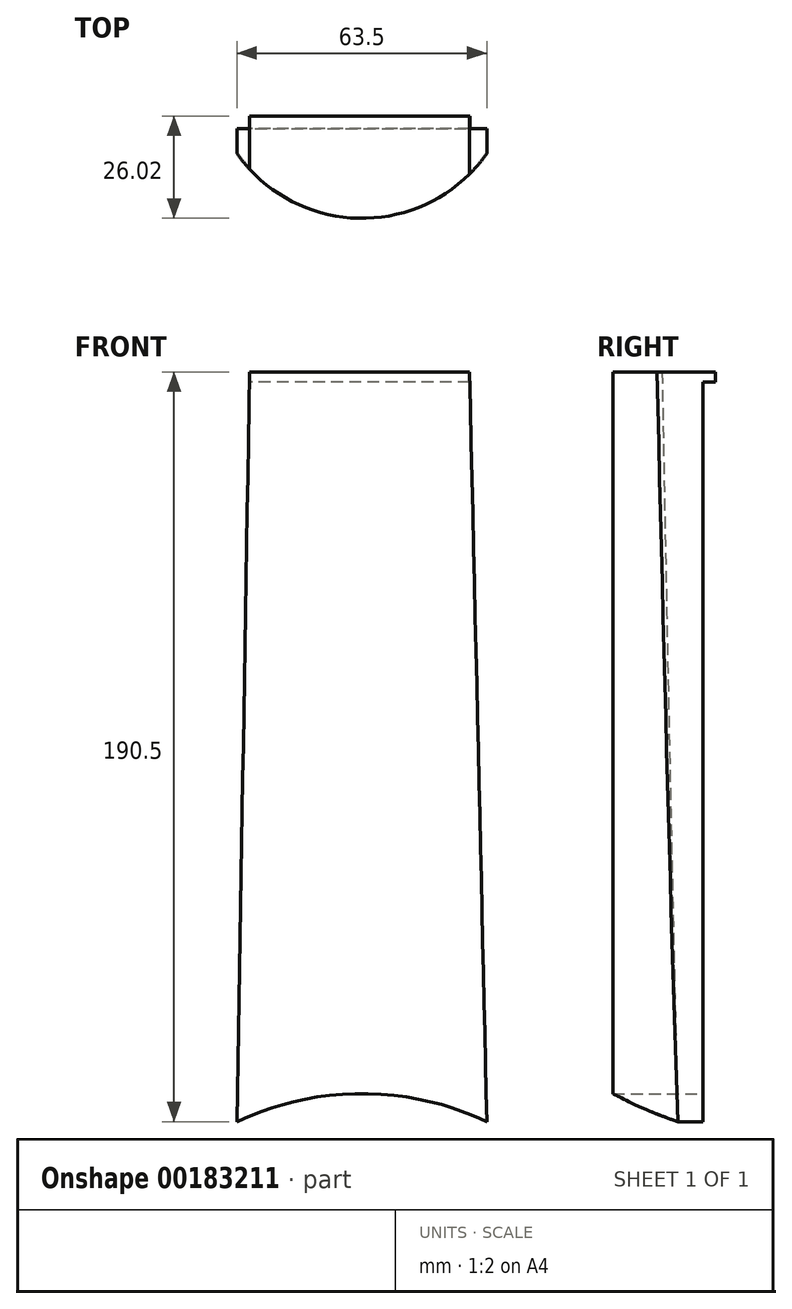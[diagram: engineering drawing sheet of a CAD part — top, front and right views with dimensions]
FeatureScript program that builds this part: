
annotation { "Feature Type Name" : "Feature", "Feature Type Description" : "" }
export const myFeature = defineFeature(function(context is Context, id is Id, definition is map)
    precondition{}
    {
        {
            var Q0;
            Q0=qCreatedBy(makeId("Top.planeOp"),FACE);
            var sketch = newSketch(context, id + "F0", { "sketchPlane" : qUnion([Q0])});
            skLineSegment(sketch, "E0.bottom", {"start": v(-12.13, 0) * mm, "end": v(51.37, 0) * mm});
            skLineSegment(sketch, "E0.top", {"start": v(-12.13, 6.35) * mm, "end": v(51.37, 6.35) * mm});
            skLineSegment(sketch, "E0.left", {"start": v(-12.13, 0) * mm, "end": v(-12.13, 6.35) * mm});
            skLineSegment(sketch, "E0.right", {"start": v(51.37, 0) * mm, "end": v(51.37, 6.35) * mm});
            skArc(sketch, "E1", {"start": v(-12.13, 0) * mm, "mid": v(19.62, -16.5) * mm, "end": v(51.37, 0) * mm});
            skSolve(sketch);
        }
        {
            var Q0;
            Q0=makeQuery(id+"F0.imprint","IMPRINT",FACE,{"disambiguationData":[TD([[makeQuery(id+"F0.imprint","IMPRINT",EDGE,{"derivedFrom":sQuery(id+"F0.wireOp",EDGE,"E0.bottom")}),-1.0]])]});
            var Q1;
            Q1=makeQuery(id+"F0.imprint","IMPRINT",FACE,{"disambiguationData":[TD([[makeQuery(id+"F0.imprint","IMPRINT",EDGE,{"derivedFrom":sQuery(id+"F0.wireOp",EDGE,"E0.bottom")}),1.0]])]});
            extrude(context, id + "F1", {"entities" : qUnion([Q0, Q1]), "depth" : 190.5 * mm});
        }
        {
            var Q0;
            Q0=makeQuery(id+"F1.opExtrude","SWEPT_FACE",FACE,{"disambiguationData":[OSD([sQuery(id+"F0.wireOp",EDGE,"E0.top")])]});
            var sketch = newSketch(context, id + "F2", { "sketchPlane" : qUnion([Q0])});
            skLineSegment(sketch, "E2", {"start": v(-51.37, 0) * mm, "end": v(-46.95, 190.5) * mm});
            skLineSegment(sketch, "E3", {"start": v(-46.95, 190.5) * mm, "end": v(8.92, 190.5) * mm});
            skLineSegment(sketch, "E4", {"start": v(8.92, 190.5) * mm, "end": v(12.13, 0) * mm});
            skSolve(sketch);
        }
        {
            var Q0;
            Q0 = qSketchRegion(id + "F2", true);
            var Q1;
            {var subQ0=sQuery(id+"F2.wireOp",EDGE,"E2");Q1=makeQuery(id+"F2.imprint","IMPRINT",FACE,{"disambiguationData":[TD([[makeQuery(id+"F2.imprint","IMPRINT",EDGE,{"derivedFrom":subQ0}),1.0]])]});}
            var Q2;
            {var subQ0=sQuery(id+"F2.wireOp",EDGE,"E4");Q2=makeQuery(id+"F2.imprint","IMPRINT",FACE,{"disambiguationData":[TD([[makeQuery(id+"F2.imprint","IMPRINT",EDGE,{"derivedFrom":subQ0}),1.0]])]});}
            extrude(context, id + "F3", {"entities" : qUnion([Q0, Q1, Q2]), "operationType" : NewBodyOperationType.REMOVE, "oppositeDirection" : true, "depth" : 25.4 * mm});
        }
        {
            var Q0;
            Q0=makeQuery(id+"F1.opExtrude","SWEPT_FACE",FACE,{"disambiguationData":[OSD([sQuery(id+"F0.wireOp",EDGE,"E0.top")])]});
            var sketch = newSketch(context, id + "F4", { "sketchPlane" : qUnion([Q0])});
            skArc(sketch, "E5", {"start": v(12.13, 0) * mm, "mid": v(-19.62, 7.1) * mm, "end": v(-51.37, 0) * mm});
            skLineSegment(sketch, "E6", {"start": v(12.13, 0) * mm, "end": v(-51.37, 0) * mm});
            skSolve(sketch);
        }
        {
            var Q0;
            Q0=makeQuery(id+"F4.imprint","IMPRINT",FACE,{"disambiguationData":[TD([[makeQuery(id+"F4.imprint","IMPRINT",EDGE,{"derivedFrom":sQuery(id+"F4.wireOp",EDGE,"E5")}),1.0]])]});
            extrude(context, id + "F5", {"entities" : qUnion([Q0]), "operationType" : NewBodyOperationType.REMOVE, "oppositeDirection" : true, "depth" : 25.4 * mm});
        }
        {
            var Q0;
            Q0=makeQuery(id+"F1.opExtrude","SWEPT_FACE",FACE,{"disambiguationData":[OSD([sQuery(id+"F0.wireOp",EDGE,"E0.top")])]});
            var sketch = newSketch(context, id + "F6", { "sketchPlane" : qUnion([Q0])});
            skLineSegment(sketch, "E7", {"start": v(-46.95, 190.5) * mm, "end": v(-47.01, 187.96) * mm});
            skLineSegment(sketch, "E8", {"start": v(-47.01, 187.96) * mm, "end": v(8.96, 187.96) * mm});
            skLineSegment(sketch, "E9", {"start": v(8.96, 187.96) * mm, "end": v(8.92, 190.5) * mm});
            skLineSegment(sketch, "E10", {"start": v(8.92, 190.5) * mm, "end": v(-46.95, 190.5) * mm});
            skSolve(sketch);
        }
        {
            var Q0;
            Q0=makeQuery(id+"F6.imprint","IMPRINT",FACE,{"disambiguationData":[TD([[makeQuery(id+"F6.imprint","IMPRINT",EDGE,{"derivedFrom":sQuery(id+"F6.wireOp",EDGE,"E7")}),-1.0]])]});
            extrude(context, id + "F7", {"entities" : qUnion([Q0]), "operationType" : NewBodyOperationType.ADD, "depth" : 3.17 * mm});
        }
    });
